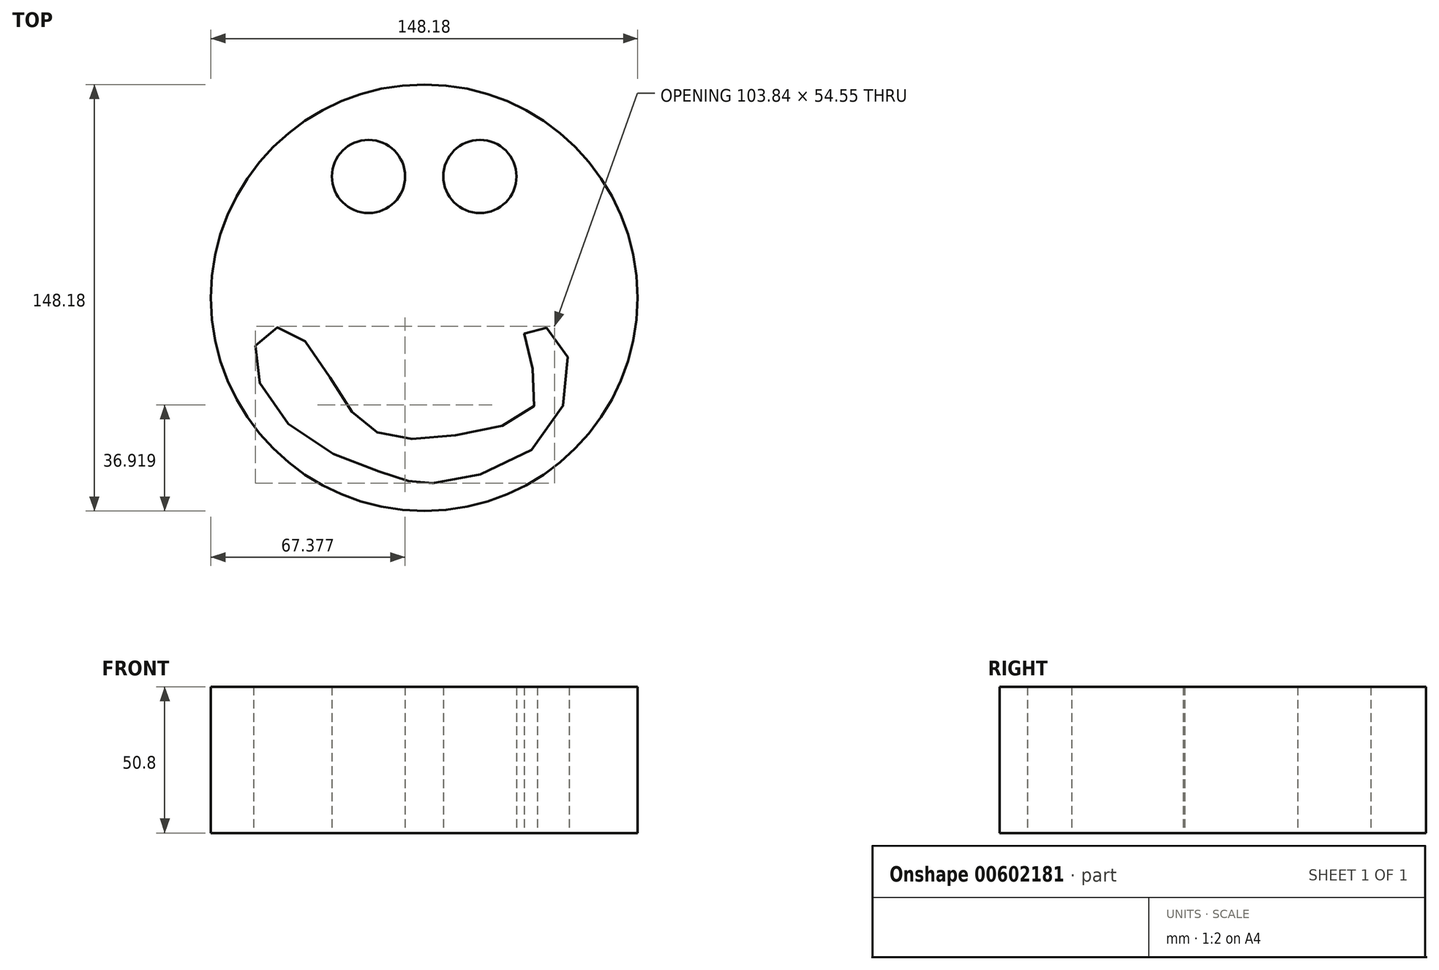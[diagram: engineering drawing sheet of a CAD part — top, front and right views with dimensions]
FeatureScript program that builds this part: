
annotation { "Feature Type Name" : "Feature", "Feature Type Description" : "" }
export const myFeature = defineFeature(function(context is Context, id is Id, definition is map)
    precondition{}
    {
        {
            var Q0;
            Q0=qCreatedBy(makeId("Top.planeOp"),FACE);
            var sketch = newSketch(context, id + "F0", { "sketchPlane" : qUnion([Q0])});
            skCircle(sketch, "E0", {"center": v(0, 0) * mm, "radius": 74.1 * mm});
            skCircle(sketch, "E1", {"center": v(-19.33, 42.13) * mm, "radius": 12.7 * mm});
            skCircle(sketch, "E2.MirrorC", {"center": v(19.33, 42.13) * mm, "radius": 12.7 * mm});
            skFitSpline(sketch, "E3", {"points": [v(-58.63, -16.66) * mm, v(-44.48, -46.21) * mm, v(-8.65, -62.56) * mm, v(0, -64.45) * mm, v(41.34, -49.04) * mm, v(46.37, -13.2) * mm, v(35.05, -11.63) * mm, v(39.14, -34.9) * mm, v(14.93, -47.16) * mm, v(-14.62, -47.47) * mm, v(-29.4, -33.32) * mm, v(-47.31, -10.69) * mm, v(-58.63, -16.66) * mm]});
            skSolve(sketch);
        }
        {
            var Q0;
            Q0=makeQuery(id+"F0.imprint","IMPRINT",FACE,{"disambiguationData":[TD([[makeQuery(id+"F0.imprint","IMPRINT",EDGE,{"derivedFrom":sQuery(id+"F0.wireOp",EDGE,"E0")}),1.0]])]});
            extrude(context, id + "F1", {"entities" : qUnion([Q0]), "depth" : 50.8 * mm, "offsetDistance" : 25.4 * mm});
        }
    });
